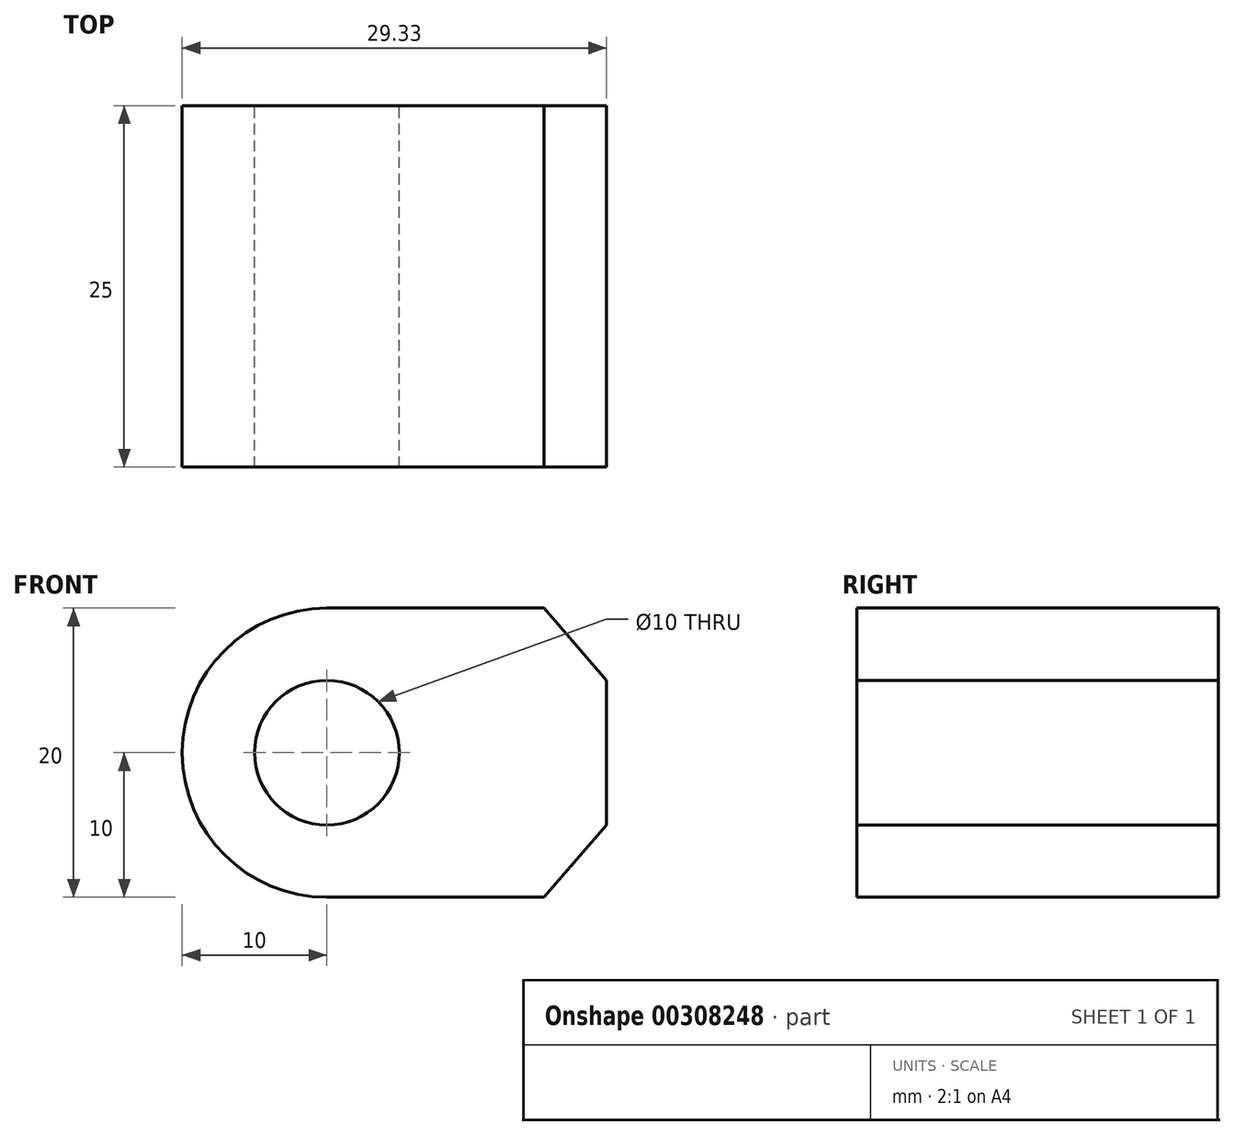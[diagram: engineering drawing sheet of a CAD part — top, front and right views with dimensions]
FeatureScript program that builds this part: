
annotation { "Feature Type Name" : "Feature", "Feature Type Description" : "" }
export const myFeature = defineFeature(function(context is Context, id is Id, definition is map)
    precondition{}
    {
        {
            var Q0;
            Q0=qCreatedBy(makeId("Front.planeOp"),FACE);
            var sketch = newSketch(context, id + "F0", { "sketchPlane" : qUnion([Q0])});
            skCircle(sketch, "E0", {"center": v(0, 0) * mm, "radius": 5 * mm});
            skLineSegment(sketch, "E1", {"start": v(4.33, -2.5) * mm, "end": v(19.33, -2.5) * mm});
            skLineSegment(sketch, "E2", {"start": v(4.33, 2.5) * mm, "end": v(19.33, 2.5) * mm});
            skLineSegment(sketch, "E3", {"start": v(19.33, -2.5) * mm, "end": v(19.33, 2.5) * mm});
            skArc(sketch, "E4", {"start": v(9.68, 2.5) * mm, "mid": v(-10, 0) * mm, "end": v(9.68, -2.5) * mm});
            skLineSegment(sketch, "E5", {"start": v(0, 10) * mm, "end": v(15, 10) * mm});
            skLineSegment(sketch, "E6", {"start": v(0, -10) * mm, "end": v(15, -10) * mm});
            skLineSegment(sketch, "E7", {"start": v(-4.33, 2.5) * mm, "end": v(-9.68, 2.5) * mm});
            skLineSegment(sketch, "E8", {"start": v(-4.33, -2.5) * mm, "end": v(-9.68, -2.5) * mm});
            skLineSegment(sketch, "E9", {"start": v(19.33, 2.5) * mm, "end": v(19.33, 5) * mm});
            skLineSegment(sketch, "E10", {"start": v(15, 10) * mm, "end": v(19.33, 5) * mm});
            skLineSegment(sketch, "E11", {"start": v(19.33, -2.5) * mm, "end": v(19.33, -5) * mm});
            skLineSegment(sketch, "E12", {"start": v(19.33, -5) * mm, "end": v(15, -10) * mm});
            skSolve(sketch);
        }
        {
            var Q0;
            {var subQ6=sQuery(id+"F0.wireOp",EDGE,"E7");Q0=makeQuery(id+"F0.imprint","IMPRINT",FACE,{"disambiguationData":[TD([[makeQuery(id+"F0.imprint","IMPRINT",EDGE,{"derivedFrom":subQ6}),-1.0]])]});}
            var Q1;
            Q1 = qSketchRegion(id + "F0", true);
            extrude(context, id + "F1", {"entities" : qUnion([Q0, Q1]), "depth" : 25 * mm});
        }
    });
